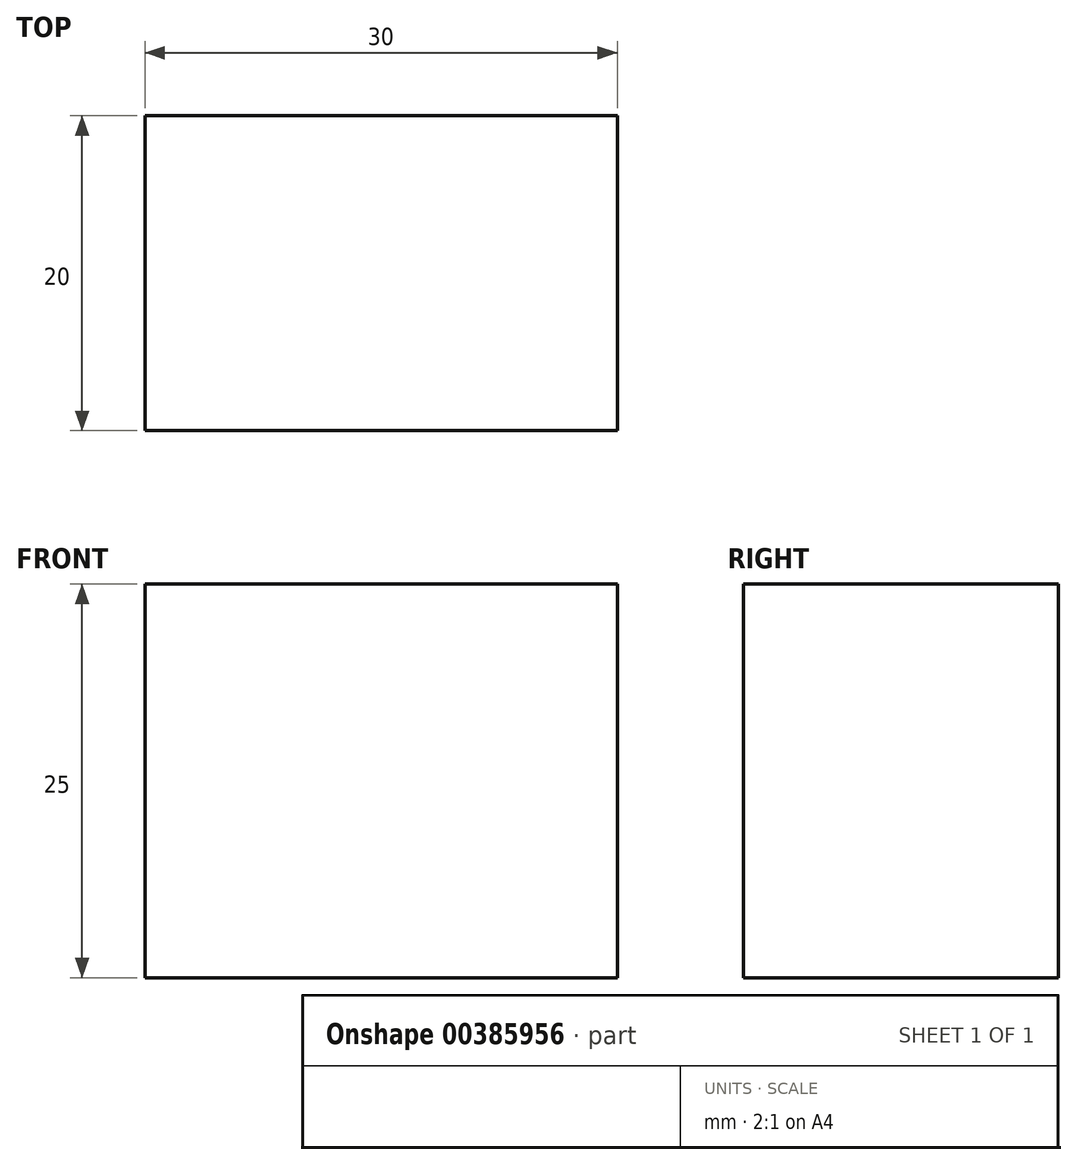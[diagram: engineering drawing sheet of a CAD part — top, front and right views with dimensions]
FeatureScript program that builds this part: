
annotation { "Feature Type Name" : "Feature", "Feature Type Description" : "" }
export const myFeature = defineFeature(function(context is Context, id is Id, definition is map)
    precondition{}
    {
        {
            var Q0;
            Q0=qCreatedBy(makeId("Top.planeOp"),FACE);
            var sketch = newSketch(context, id + "F0", { "sketchPlane" : qUnion([Q0])});
            skLineSegment(sketch, "E0.bottom", {"start": v(15, -10) * mm, "end": v(-15, -10) * mm});
            skLineSegment(sketch, "E0.top", {"start": v(15, 10) * mm, "end": v(-15, 10) * mm});
            skLineSegment(sketch, "E0.left", {"start": v(15, -10) * mm, "end": v(15, 10) * mm});
            skLineSegment(sketch, "E0.right", {"start": v(-15, -10) * mm, "end": v(-15, 10) * mm});
            skPoint(sketch, "E0.middle", {"position": v(0, 0) * mm});
            skSolve(sketch);
        }
        {
            var Q0;
            Q0 = qSketchRegion(id + "F0", true);
            extrude(context, id + "F1", {"entities" : qUnion([Q0]), "depth" : 25 * mm});
        }
    });
